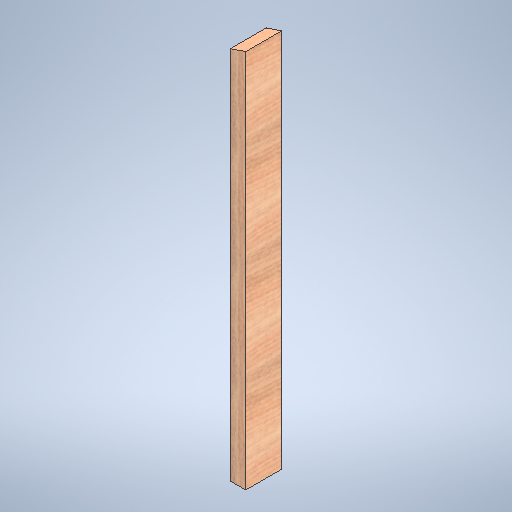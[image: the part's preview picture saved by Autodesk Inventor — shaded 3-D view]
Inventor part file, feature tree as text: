
AUTODESK INVENTOR PART (.ipt)
format: ipt  version: 2025.1 (Build 291241020, 241B)  size: 322,560 bytes
history: native  units: in
note: dims shown in document units (in); Inventor stores cm internally (conversion verified against a paired STEP export)
features: extrude x1, sketch x1
ambient origin geometry x8: Origin, YZ Plane, XZ Plane, XY Plane, X Axis, Y Axis, Z Axis, Center Point
bodies: Solid1 (feature_tree)
feature tree (2):
  extrude  "Extrusion1"  Depth=3.5in TaperAngle=0.0deg
  sketch  "Sketch1"  dims[d2=1.5in d3=3.5in d4=0.0in d5=36.578in d6=37.078in]
